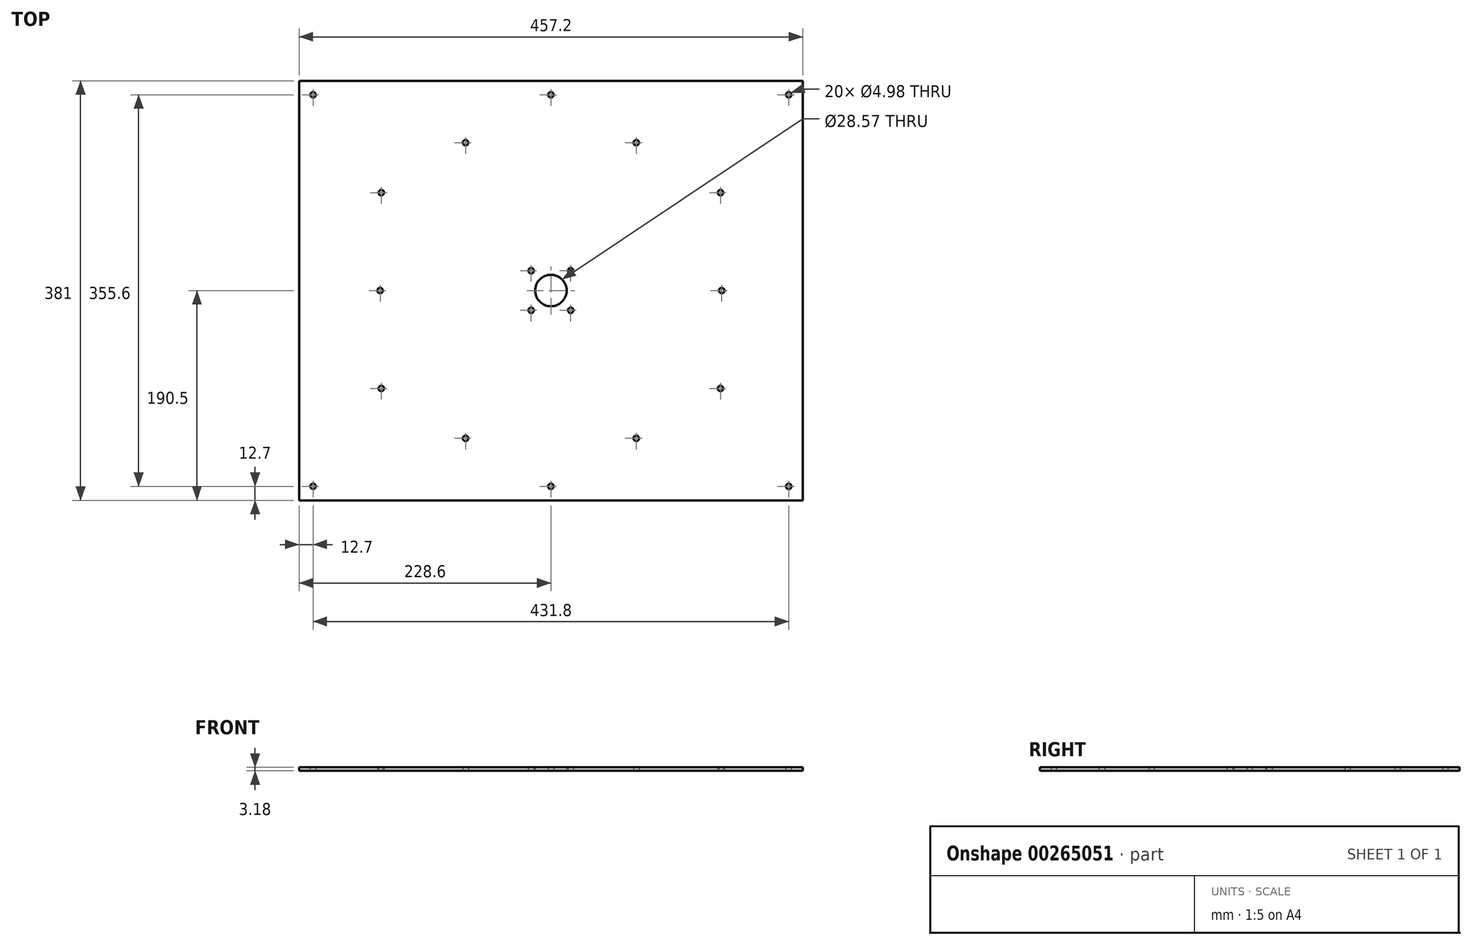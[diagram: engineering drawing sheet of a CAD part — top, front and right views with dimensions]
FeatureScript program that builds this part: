
annotation { "Feature Type Name" : "Feature", "Feature Type Description" : "" }
export const myFeature = defineFeature(function(context is Context, id is Id, definition is map)
    precondition{}
    {
        {
            var Q0;
            Q0=qCreatedBy(makeId("Top.planeOp"),FACE);
            var sketch = newSketch(context, id + "F0", { "sketchPlane" : qUnion([Q0])});
            skLineSegment(sketch, "E0.bottom", {"start": v(0, 0) * mm, "end": v(457.2, 0) * mm});
            skLineSegment(sketch, "E0.top", {"start": v(0, 381) * mm, "end": v(457.2, 381) * mm});
            skLineSegment(sketch, "E0.left", {"start": v(0, 0) * mm, "end": v(0, 381) * mm});
            skLineSegment(sketch, "E0.right", {"start": v(457.2, 0) * mm, "end": v(457.2, 381) * mm});
            skCircle(sketch, "E1", {"center": v(228.6, 190.5) * mm, "radius": 50.8 * mm, "construction": true});
            skLineSegment(sketch, "E2", {"start": v(228.6, 190.5) * mm, "end": v(228.6, 0) * mm, "construction": true});
            skLineSegment(sketch, "E3", {"start": v(228.6, 190.5) * mm, "end": v(0, 190.5) * mm, "construction": true});
            skCircle(sketch, "E4.cCircle", {"center": v(228.6, 190.5) * mm, "radius": 134.25 * mm, "construction": true});
            skLineSegment(sketch, "E4.0", {"start": v(73.58, 190.5) * mm, "end": v(151.09, 324.75) * mm, "construction": true});
            skLineSegment(sketch, "E4.1", {"start": v(151.09, 324.75) * mm, "end": v(306.11, 324.75) * mm, "construction": true});
            skLineSegment(sketch, "E4.2", {"start": v(306.11, 324.75) * mm, "end": v(383.62, 190.5) * mm, "construction": true});
            skLineSegment(sketch, "E4.3", {"start": v(383.62, 190.5) * mm, "end": v(306.11, 56.25) * mm, "construction": true});
            skLineSegment(sketch, "E4.4", {"start": v(306.11, 56.25) * mm, "end": v(151.09, 56.25) * mm, "construction": true});
            skLineSegment(sketch, "E4.5", {"start": v(151.09, 56.25) * mm, "end": v(73.58, 190.5) * mm, "construction": true});
            skPoint(sketch, "E4.0.midPoint", {"position": v(112.33, 257.63) * mm});
            skCircle(sketch, "E5", {"center": v(151.09, 324.75) * mm, "radius": 38.1 * mm, "construction": true});
            skCircle(sketch, "E6", {"center": v(306.11, 324.75) * mm, "radius": 38.1 * mm, "construction": true});
            skCircle(sketch, "E7", {"center": v(383.62, 190.5) * mm, "radius": 38.1 * mm, "construction": true});
            skCircle(sketch, "E8", {"center": v(306.11, 56.25) * mm, "radius": 38.1 * mm, "construction": true});
            skCircle(sketch, "E9", {"center": v(151.09, 56.25) * mm, "radius": 38.1 * mm, "construction": true});
            skCircle(sketch, "E10", {"center": v(73.58, 190.5) * mm, "radius": 38.1 * mm, "construction": true});
            skLineSegment(sketch, "E11", {"start": v(95.43, 159.29) * mm, "end": v(199.47, 232.12) * mm, "construction": true});
            skCircle(sketch, "E12", {"center": v(151.09, 324.75) * mm, "radius": 2.49 * mm});
            skCircle(sketch, "E13", {"center": v(306.11, 324.75) * mm, "radius": 2.49 * mm});
            skCircle(sketch, "E14", {"center": v(383.62, 190.5) * mm, "radius": 2.49 * mm});
            skCircle(sketch, "E15", {"center": v(306.11, 56.25) * mm, "radius": 2.49 * mm});
            skCircle(sketch, "E16", {"center": v(151.09, 56.25) * mm, "radius": 2.49 * mm});
            skCircle(sketch, "E17", {"center": v(73.58, 190.5) * mm, "radius": 2.49 * mm});
            skCircle(sketch, "E18", {"center": v(228.6, 190.5) * mm, "radius": 14.29 * mm});
            skCircle(sketch, "E19.cCircle", {"center": v(228.6, 190.5) * mm, "radius": 17.96 * mm, "construction": true});
            skLineSegment(sketch, "E19.0", {"start": v(246.56, 208.46) * mm, "end": v(246.56, 172.54) * mm, "construction": true});
            skLineSegment(sketch, "E19.1", {"start": v(246.56, 172.54) * mm, "end": v(210.64, 172.54) * mm, "construction": true});
            skLineSegment(sketch, "E19.2", {"start": v(210.64, 172.54) * mm, "end": v(210.64, 208.46) * mm, "construction": true});
            skLineSegment(sketch, "E19.3", {"start": v(210.64, 208.46) * mm, "end": v(246.56, 208.46) * mm, "construction": true});
            skPoint(sketch, "E19.0.midPoint", {"position": v(246.56, 190.5) * mm});
            skCircle(sketch, "E20", {"center": v(210.64, 208.46) * mm, "radius": 2.49 * mm});
            skCircle(sketch, "E21", {"center": v(246.56, 208.46) * mm, "radius": 2.49 * mm});
            skCircle(sketch, "E22", {"center": v(210.64, 172.54) * mm, "radius": 2.49 * mm});
            skCircle(sketch, "E23", {"center": v(246.56, 172.54) * mm, "radius": 2.49 * mm});
            skCircle(sketch, "E24.cCircle", {"center": v(228.6, 190.5) * mm, "radius": 153.98 * mm, "construction": true});
            skLineSegment(sketch, "E24.0", {"start": v(74.62, 279.4) * mm, "end": v(228.6, 368.3) * mm, "construction": true});
            skLineSegment(sketch, "E24.1", {"start": v(228.6, 368.3) * mm, "end": v(382.58, 279.4) * mm, "construction": true});
            skLineSegment(sketch, "E24.2", {"start": v(382.58, 279.4) * mm, "end": v(382.58, 101.6) * mm, "construction": true});
            skLineSegment(sketch, "E24.3", {"start": v(382.58, 101.6) * mm, "end": v(228.6, 12.7) * mm, "construction": true});
            skLineSegment(sketch, "E24.4", {"start": v(228.6, 12.7) * mm, "end": v(74.62, 101.6) * mm, "construction": true});
            skLineSegment(sketch, "E24.5", {"start": v(74.62, 101.6) * mm, "end": v(74.62, 279.4) * mm, "construction": true});
            skPoint(sketch, "E24.0.midPoint", {"position": v(151.09, 323.55) * mm});
            skCircle(sketch, "E25", {"center": v(74.62, 279.4) * mm, "radius": 2.49 * mm});
            skCircle(sketch, "E26", {"center": v(228.6, 368.3) * mm, "radius": 2.49 * mm});
            skCircle(sketch, "E27", {"center": v(382.58, 279.4) * mm, "radius": 2.49 * mm});
            skCircle(sketch, "E28", {"center": v(382.58, 101.6) * mm, "radius": 2.49 * mm});
            skCircle(sketch, "E29", {"center": v(228.6, 12.7) * mm, "radius": 2.49 * mm});
            skCircle(sketch, "E30", {"center": v(74.62, 101.6) * mm, "radius": 2.49 * mm});
            skPoint(sketch, "E31.0.midPoint", {"position": v(140.04, 190.5) * mm});
            skSolve(sketch);
        }
        {
            var Q0;
            Q0=makeQuery(id+"F0.imprint","IMPRINT",FACE,{"disambiguationData":[TD([[makeQuery(id+"F0.imprint","IMPRINT",EDGE,{"derivedFrom":sQuery(id+"F0.wireOp",EDGE,"E0.bottom")}),1.0]])]});
            extrude(context, id + "F1", {"entities" : qUnion([Q0]), "depth" : 3.17 * mm});
        }
        {
            var Q0;
            Q0=makeQuery(id+"F1.opExtrude","CAP_FACE",FACE,{"disambiguationData":[OSD([sQuery(id+"F0.wireOp",EDGE,"E0.bottom"),sQuery(id+"F0.wireOp",EDGE,"E0.top"),sQuery(id+"F0.wireOp",EDGE,"E0.left"),sQuery(id+"F0.wireOp",EDGE,"E0.right"),sQuery(id+"F0.wireOp",EDGE,"E12"),sQuery(id+"F0.wireOp",EDGE,"E13"),sQuery(id+"F0.wireOp",EDGE,"E14"),sQuery(id+"F0.wireOp",EDGE,"E15"),sQuery(id+"F0.wireOp",EDGE,"E16"),sQuery(id+"F0.wireOp",EDGE,"E17"),sQuery(id+"F0.wireOp",EDGE,"E18"),sQuery(id+"F0.wireOp",EDGE,"E20"),sQuery(id+"F0.wireOp",EDGE,"E21"),sQuery(id+"F0.wireOp",EDGE,"E22"),sQuery(id+"F0.wireOp",EDGE,"E23"),sQuery(id+"F0.wireOp",EDGE,"E25"),sQuery(id+"F0.wireOp",EDGE,"E26"),sQuery(id+"F0.wireOp",EDGE,"E27"),sQuery(id+"F0.wireOp",EDGE,"E28"),sQuery(id+"F0.wireOp",EDGE,"E29"),sQuery(id+"F0.wireOp",EDGE,"E30")])],"isStart":false});
            var sketch = newSketch(context, id + "F2", { "sketchPlane" : qUnion([Q0])});
            skCircle(sketch, "E32.0", {"center": v(228.6, 190.5) * mm, "radius": 14.29 * mm, "construction": true});
            skCircle(sketch, "E33.cCircle", {"center": v(228.6, 190.5) * mm, "radius": 71.5 * mm, "construction": true});
            skLineSegment(sketch, "E33.0", {"start": v(157.1, 149.23) * mm, "end": v(157.1, 231.78) * mm, "construction": true});
            skLineSegment(sketch, "E33.1", {"start": v(157.1, 231.78) * mm, "end": v(228.6, 273.05) * mm, "construction": true});
            skLineSegment(sketch, "E33.2", {"start": v(228.6, 273.05) * mm, "end": v(300.1, 231.78) * mm, "construction": true});
            skLineSegment(sketch, "E33.3", {"start": v(300.1, 231.78) * mm, "end": v(300.1, 149.23) * mm, "construction": true});
            skLineSegment(sketch, "E33.4", {"start": v(300.1, 149.23) * mm, "end": v(228.6, 107.95) * mm, "construction": true});
            skLineSegment(sketch, "E33.5", {"start": v(228.6, 107.95) * mm, "end": v(157.1, 149.23) * mm, "construction": true});
            skPoint(sketch, "E33.0.midPoint", {"position": v(157.1, 190.5) * mm});
            skCircle(sketch, "E34", {"center": v(228.6, 190.5) * mm, "radius": 50.8 * mm, "construction": true});
            skLineSegment(sketch, "E35", {"start": v(228.6, 241.3) * mm, "end": v(537.61, 241.3) * mm, "construction": true});
            skCircle(sketch, "E36", {"center": v(12.7, 368.3) * mm, "radius": 2.49 * mm});
            skCircle(sketch, "E37", {"center": v(444.5, 368.3) * mm, "radius": 2.49 * mm});
            skCircle(sketch, "E38", {"center": v(444.5, 12.7) * mm, "radius": 2.49 * mm});
            skCircle(sketch, "E39", {"center": v(12.7, 12.7) * mm, "radius": 2.49 * mm});
            skLineSegment(sketch, "E40.0.0", {"start": v(457.2, 381) * mm, "end": v(0, 381) * mm, "construction": true});
            skLineSegment(sketch, "E40.0.1", {"start": v(0, 381) * mm, "end": v(0, 0) * mm, "construction": true});
            skLineSegment(sketch, "E40.0.2", {"start": v(0, 0) * mm, "end": v(457.2, 0) * mm, "construction": true});
            skLineSegment(sketch, "E40.0.3", {"start": v(457.2, 0) * mm, "end": v(457.2, 381) * mm, "construction": true});
            skCircle(sketch, "E41.0", {"center": v(228.6, 368.3) * mm, "radius": 2.49 * mm, "construction": true});
            skSolve(sketch);
        }
        {
            var Q0;
            Q0 = qSketchRegion(id + "F2", true);
            extrude(context, id + "F3", {"entities" : qUnion([Q0]), "operationType" : NewBodyOperationType.REMOVE, "endBound" : BoundingType.THROUGH_ALL, "oppositeDirection" : true, "depth" : 25.4 * mm});
        }
    });
